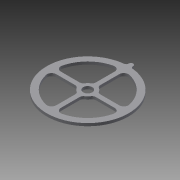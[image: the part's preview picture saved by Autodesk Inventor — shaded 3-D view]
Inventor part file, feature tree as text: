
AUTODESK INVENTOR PART (.ipt)
format: ipt  version: 2013 (Build 170138000, 138)  size: 154,624 bytes
history: native  units: mm
features: extrude x1, sketch x1
ambient origin geometry x8: Origin, YZ Plane, XZ Plane, XY Plane, X Axis, Y Axis, Z Axis, Center Point
feature tree (2):
  extrude  "Extrusion2"  Depth=76.2mm
  sketch  "Sketch1"  dims[d0=90.0mm d1=76.2mm d2=2.5mm d3=2.5mm d4=2.5mm d5=2.5mm d7=2.5mm d8=2.5mm d9=2.5mm d10=5.0mm d11=5.0mm d12=5.0mm d13=5.0mm d14=38.1mm d15=38.1mm d16=38.1mm d17=38.1mm d18=5.0mm d19=5.0mm d20=50.0mm d21=2.5mm d24=10.0mm d26=18.0mm d27=4.0mm d28=3.0mm d29=0.0mm]
